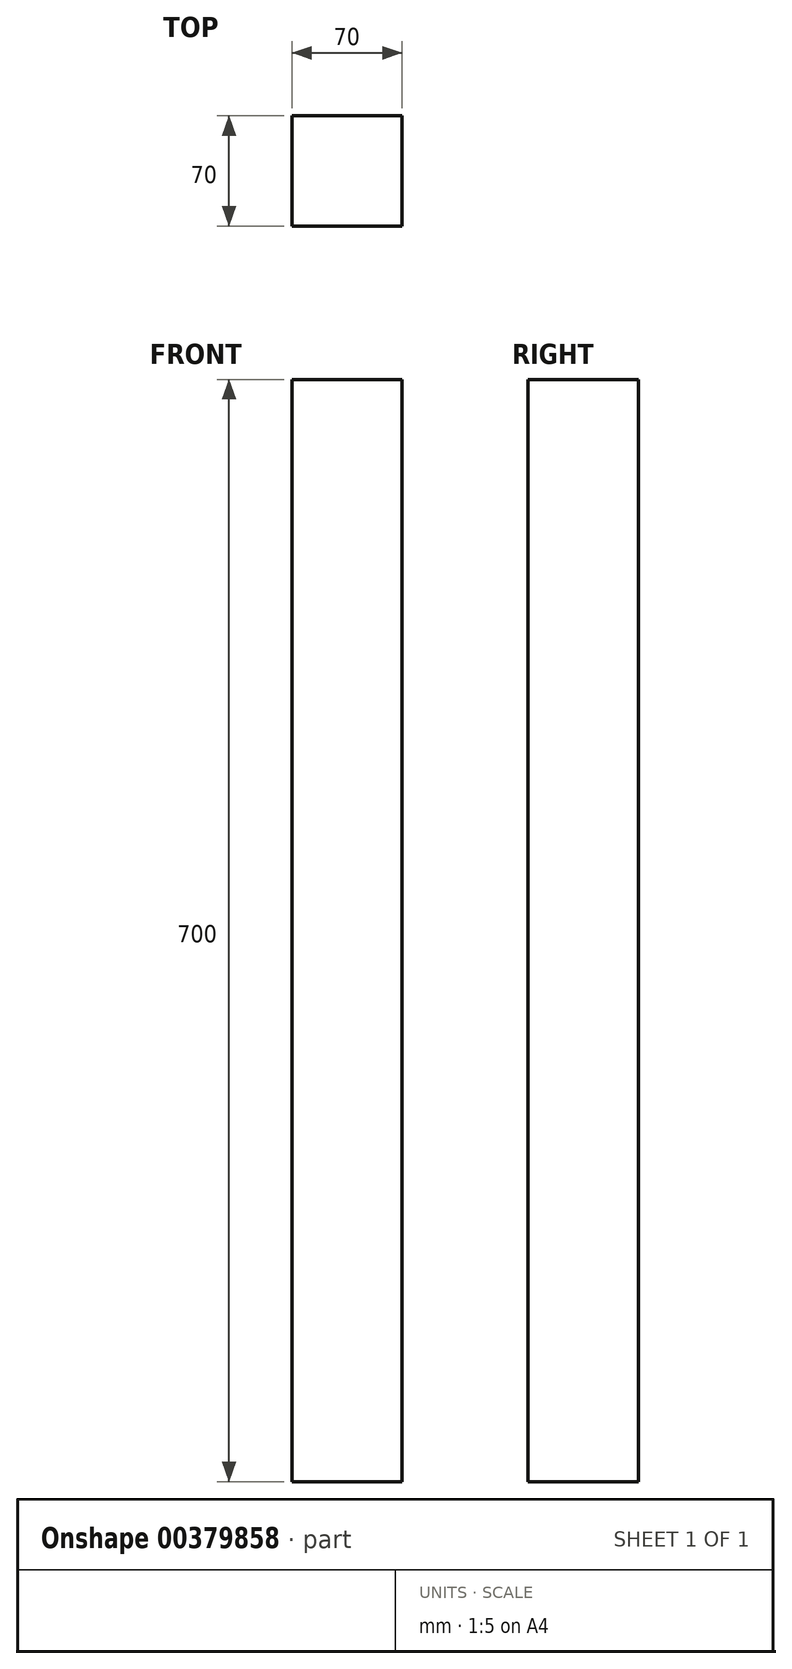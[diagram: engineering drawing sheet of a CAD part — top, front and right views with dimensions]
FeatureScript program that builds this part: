
annotation { "Feature Type Name" : "Feature", "Feature Type Description" : "" }
export const myFeature = defineFeature(function(context is Context, id is Id, definition is map)
    precondition{}
    {
        {
            var Q0;
            Q0=qCreatedBy(makeId("Top.planeOp"),FACE);
            var sketch = newSketch(context, id + "F0", { "sketchPlane" : qUnion([Q0])});
            skLineSegment(sketch, "E0.bottom", {"start": v(35, -35) * mm, "end": v(-35, -35) * mm});
            skLineSegment(sketch, "E0.top", {"start": v(35, 35) * mm, "end": v(-35, 35) * mm});
            skLineSegment(sketch, "E0.left", {"start": v(35, -35) * mm, "end": v(35, 35) * mm});
            skLineSegment(sketch, "E0.right", {"start": v(-35, -35) * mm, "end": v(-35, 35) * mm});
            skPoint(sketch, "E0.middle", {"position": v(0, 0) * mm});
            skSolve(sketch);
        }
        {
            var Q0;
            Q0=qSketchRegion(id+"F0",true);
            extrude(context, id + "F1", {"entities" : qUnion([Q0]), "depth" : 700 * mm});
        }
    });
